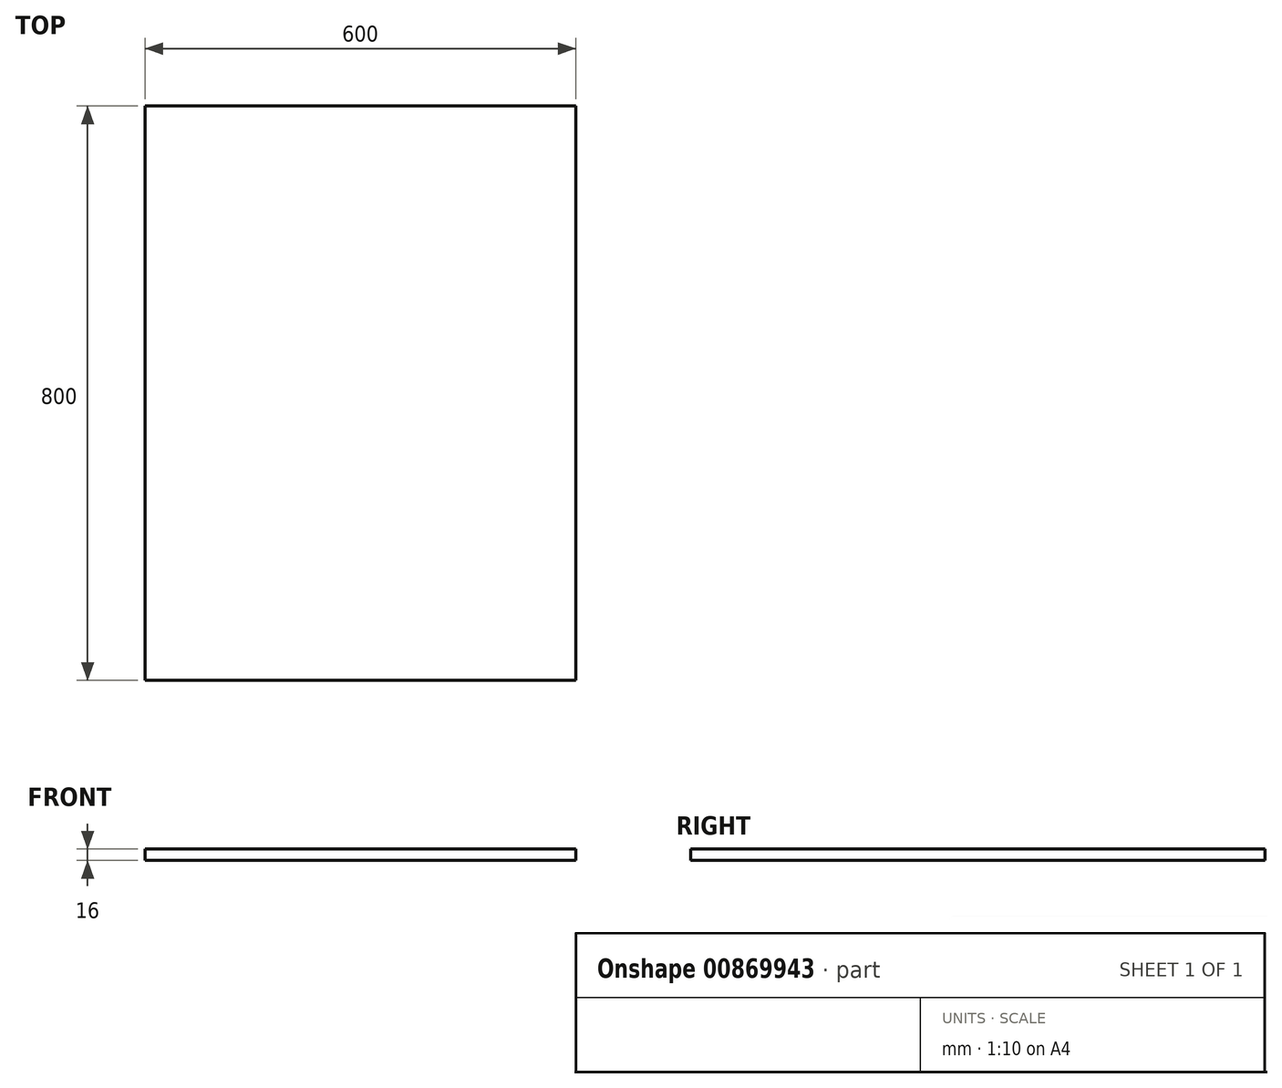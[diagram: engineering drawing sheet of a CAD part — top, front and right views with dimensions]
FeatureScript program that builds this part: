
annotation { "Feature Type Name" : "Feature", "Feature Type Description" : "" }
export const myFeature = defineFeature(function(context is Context, id is Id, definition is map)
    precondition{}
    {
        {
            var Q0;
            Q0=qCreatedBy(makeId("Top.planeOp"),FACE);
            var sketch = newSketch(context, id + "F0", { "sketchPlane" : qUnion([Q0])});
            skLineSegment(sketch, "E0.bottom", {"start": v(-300, 500) * mm, "end": v(300, 500) * mm});
            skLineSegment(sketch, "E0.top", {"start": v(-300, -300) * mm, "end": v(300, -300) * mm});
            skLineSegment(sketch, "E0.left", {"start": v(-300, 500) * mm, "end": v(-300, -300) * mm});
            skLineSegment(sketch, "E0.right", {"start": v(300, 500) * mm, "end": v(300, -300) * mm});
            skLineSegment(sketch, "E1", {"start": v(-300, 0) * mm, "end": v(300, 0) * mm, "construction": true});
            skSolve(sketch);
        }
        {
            var Q0;
            Q0=makeQuery(id+"F0.imprint","IMPRINT",FACE,{"disambiguationData":[TD([[makeQuery(id+"F0.imprint","IMPRINT",EDGE,{"derivedFrom":sQuery(id+"F0.wireOp",EDGE,"E0.bottom")}),-1.0]])]});
            extrude(context, id + "F1", {"entities" : qUnion([Q0]), "depth" : 16 * mm, "offsetDistance" : 25 * mm});
        }
    });
